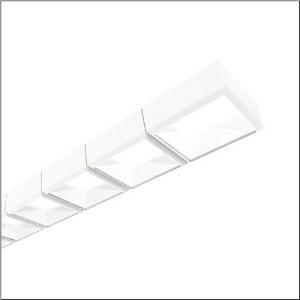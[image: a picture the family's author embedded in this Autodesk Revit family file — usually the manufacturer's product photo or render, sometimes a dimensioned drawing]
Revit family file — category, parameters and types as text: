
# Revit family: scriptus_r__11_5mz313d0twb_9c96
name_source: partatom
category: Lighting Fixtures
units: mm (PartAtom-declared; Revit-internal decimal feet)

## family parameters
Cut with Voids When Loaded = No
Host = Face
Light Source = No
Part Type = Normal
Room Calculation Point = No
Round Connector Dimension = Use Diameter
Shared = No

## types (1)
- --- (1 x LED 3000K+6500K / CRI = 80 (unbekannt), 3390 lm / 3550 lm, 3000K)
    Apparent Load = 107 VA
    CIE Flux Codes = 0 0 0 0 100 / 82 95 99 100 100
    Color Rendering = 80
    Color Temperature = 3000K
    Default Elevation = 1800 mm
    Description = Scriptus® 11, office luminaire, primary optical cover: lenses, CAT 2 (L<= 3000cd/m²), light emission: direct/indirect distribution, primary light characteristic: symmetric, installation type: suspended mounting, LED, rated luminous flux: 13.880lm, luminous efficacy: 126lm/W, light colour: 8tw, colour temperature: 3000..6500K, control gear: DALI DT8, with terminal, 5-pole, mains connection: 230V, AC, 50Hz, rated input power: 110W, LED, control gear: ECG DALI, housing, luminaire housing, of aluminium, traffic white (RAL 9016), length: 2.648mm, width: 114mm, height: 57mm, protection rating (complete): IP20, insulation class (complete): insulation class I (protective earthing), certification: CE, protection symbol: F, permissible operating ambient temperature: <= +25°C, standard: EN 50419, packaging unit: 1 piece
    Height = 57 mm
    Lamp = 1 x LED 3000K+6500K / CRI >= 80 (unbekannt)
    Lamp Light Flux = 3390 lm / 3550 lm
    Lamp count = 1
    Length = 2648 mm
    Luminous efficacy = 130 lm/W
    Manufacturer = Siteco
    ModVariant = No
    Model = 5MZ313D0TWB
    Mounting Place = Ceiling
    Mounting Type = Pendant
    Number of Poles = 1
    OnlyDefault = Yes
    Power Factor = 1
    Product Name = Scriptus® 11
    Product group = office luminaire | ceiling pendant
    ProductGroupID = 903
    Protection Class = Protection class I
    Protection Degree = IP 20
    RLX_Detail_Level = 1
    RLX_Emergency_Light_Flux = 0 lm
    RLX_Emergency_Type = 0
    RLX_Emergency_Type_DB = No
    RlxData = <blob elided: 32069 chars, md5=619051c9>
    Socket = socket
    Standby Power = 0 W
    System Light Flux = 13880 lm
    System Power = 107 W
    Type Comments = individual setting: colour temperature 6500K
    Type Image = l_1004839.jpg
    URL = http://relux.com
    VarID = @adj_219998
    Voltage = 0 V
    Weight = 0.00 kg
    Width = 114 mm

## geometry (parser evidence)
native form markers: Blend x4, Sweep x22
no freeform markers — native parametric forms only
